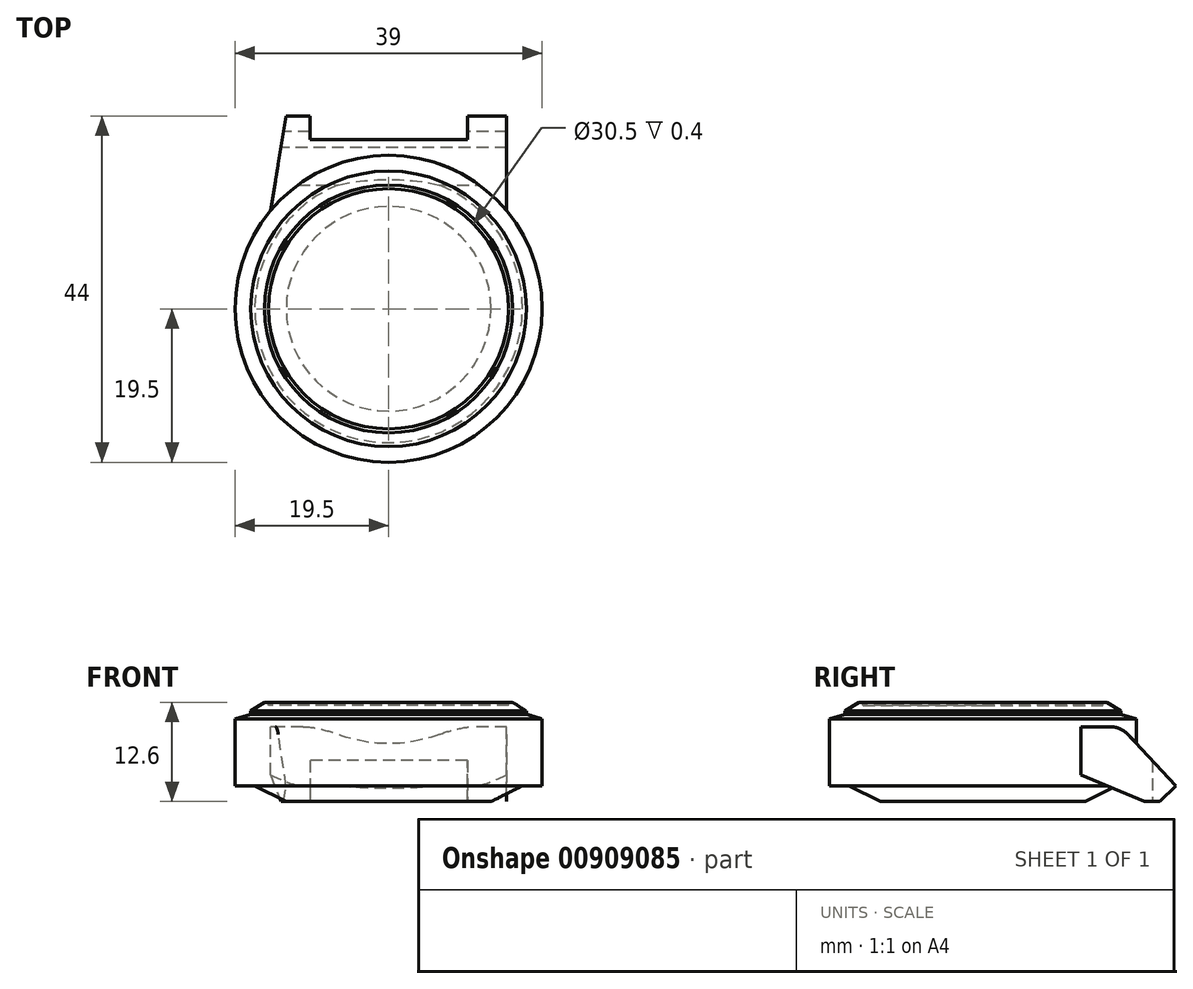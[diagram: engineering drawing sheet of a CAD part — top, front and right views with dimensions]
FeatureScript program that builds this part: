
annotation { "Feature Type Name" : "Feature", "Feature Type Description" : "" }
export const myFeature = defineFeature(function(context is Context, id is Id, definition is map)
    precondition{}
    {
        {
            var Q0;
            Q0=qCreatedBy(makeId("Front.planeOp"),FACE);
            var sketch = newSketch(context, id + "F0", { "sketchPlane" : qUnion([Q0])});
            skLineSegment(sketch, "E0", {"start": v(0, 0) * mm, "end": v(-13, 0) * mm});
            skLineSegment(sketch, "E1", {"start": v(-13, 0) * mm, "end": v(-17, 2) * mm});
            skLineSegment(sketch, "E2", {"start": v(-17, 2) * mm, "end": v(-19.5, 2) * mm});
            skLineSegment(sketch, "E3", {"start": v(-19.5, 2) * mm, "end": v(-19.5, 10.5) * mm});
            skLineSegment(sketch, "E4", {"start": v(-17.5, 11.5) * mm, "end": v(-15.75, 12.6) * mm});
            skLineSegment(sketch, "E5", {"start": v(-15.75, 12.6) * mm, "end": v(-15.25, 12.6) * mm});
            skLineSegment(sketch, "E6", {"start": v(-15.25, 12.6) * mm, "end": v(-15.25, 12.2) * mm});
            skLineSegment(sketch, "E7", {"start": v(-15.25, 12.2) * mm, "end": v(0, 12.2) * mm});
            skLineSegment(sketch, "E8", {"start": v(0, 12.2) * mm, "end": v(0, 0) * mm});
            skLineSegment(sketch, "E9", {"start": v(0, 23.3) * mm, "end": v(0, -16.5) * mm, "construction": true});
            skLineSegment(sketch, "E10", {"start": v(-19.5, 10.5) * mm, "end": v(-17.5, 11.1) * mm});
            skLineSegment(sketch, "E11", {"start": v(-17.5, 11.1) * mm, "end": v(-17.5, 11.5) * mm});
            skSolve(sketch);
        }
        {
            var Q0;
            Q0=qSketchRegion(id+"F0",true);
            var Q1;
            Q1=sQuery(id+"F0.wireOp",EDGE,"E9");
            revolve(context, id + "F1", {"surfaceOperationType" : NewSurfaceOperationType.NEW, "entities" : qUnion([Q0]), "axis" : qUnion([Q1]), "revolveType" : RevolveType.FULL});
        }
        {
            var Q0;
            Q0=qCreatedBy(makeId("Right.planeOp"),FACE);
            var sketch = newSketch(context, id + "F2", { "sketchPlane" : qUnion([Q0])});
            skLineSegment(sketch, "E12", {"start": v(22.5, 0) * mm, "end": v(20.5, 0) * mm});
            skLineSegment(sketch, "E13", {"start": v(20.5, 0) * mm, "end": v(11, 4) * mm});
            skLineSegment(sketch, "E14", {"start": v(11, 9.5) * mm, "end": v(16.2, 9.5) * mm});
            skLineSegment(sketch, "E15", {"start": v(18.39, 8.55) * mm, "end": v(24.5, 2) * mm});
            skLineSegment(sketch, "E16", {"start": v(24.5, 2) * mm, "end": v(22.5, 0) * mm});
            skLineSegment(sketch, "E17", {"start": v(11, 9.5) * mm, "end": v(11, 4) * mm});
            skPoint(sketch, "E18.visualSharp", {"position": v(17.5, 9.5) * mm});
            skArc(sketch, "E18.filletArc", {"start": v(18.39, 8.55) * mm, "mid": v(17.4, 9.25) * mm, "end": v(16.2, 9.5) * mm});
            skSolve(sketch);
        }
        {
            var Q0;
            Q0=qSketchRegion(id+"F2",true);
            extrude(context, id + "F3", {"entities" : qUnion([Q0]), "operationType" : NewBodyOperationType.ADD, "endBound" : BoundingType.SYMMETRIC, "depth" : 30 * mm, "offsetDistance" : 25 * mm});
        }
        {
            var Q0;
            Q0=qCreatedBy(makeId("Top.planeOp"),FACE);
            var sketch = newSketch(context, id + "F4", { "sketchPlane" : qUnion([Q0])});
            skLineSegment(sketch, "E19.0", {"start": v(-15, 12.46) * mm, "end": v(-15, 24.5) * mm});
            skLineSegment(sketch, "E20.0", {"start": v(-13, 24.5) * mm, "end": v(-15, 24.5) * mm});
            skLineSegment(sketch, "E21", {"start": v(-15, 12.46) * mm, "end": v(-13, 24.5) * mm});
            skPoint(sketch, "E22.orphan", {"position": v(-15, 16.2) * mm});
            skPoint(sketch, "E23.orphan", {"position": v(15, 24.5) * mm});
            skSolve(sketch);
        }
        {
            var Q0;
            Q0=qSketchRegion(id+"F4",true);
            extrude(context, id + "F5", {"entities" : qUnion([Q0]), "operationType" : NewBodyOperationType.REMOVE, "endBound" : BoundingType.THROUGH_ALL, "depth" : 25 * mm, "offsetDistance" : 25 * mm});
        }
        {
            var Q0;
            Q0=qCreatedBy(makeId("Top.planeOp"),FACE);
            var sketch = newSketch(context, id + "F6", { "sketchPlane" : qUnion([Q0])});
            skLineSegment(sketch, "E24.0", {"start": v(10, 24.5) * mm, "end": v(-10, 24.5) * mm});
            skLineSegment(sketch, "E25", {"start": v(-10, 24.5) * mm, "end": v(-10, 21.5) * mm});
            skLineSegment(sketch, "E26", {"start": v(-10, 21.5) * mm, "end": v(10, 21.5) * mm});
            skLineSegment(sketch, "E27", {"start": v(10, 21.5) * mm, "end": v(10, 24.5) * mm});
            skPoint(sketch, "E28.orphan", {"position": v(13, 24.5) * mm});
            skPoint(sketch, "E29.orphan", {"position": v(-13, 24.5) * mm});
            skSolve(sketch);
        }
        {
            var Q0;
            Q0=qSketchRegion(id+"F6",true);
            extrude(context, id + "F7", {"entities" : qUnion([Q0]), "operationType" : NewBodyOperationType.REMOVE, "endBound" : BoundingType.THROUGH_ALL, "depth" : 25 * mm, "offsetDistance" : 25 * mm});
        }
    });
